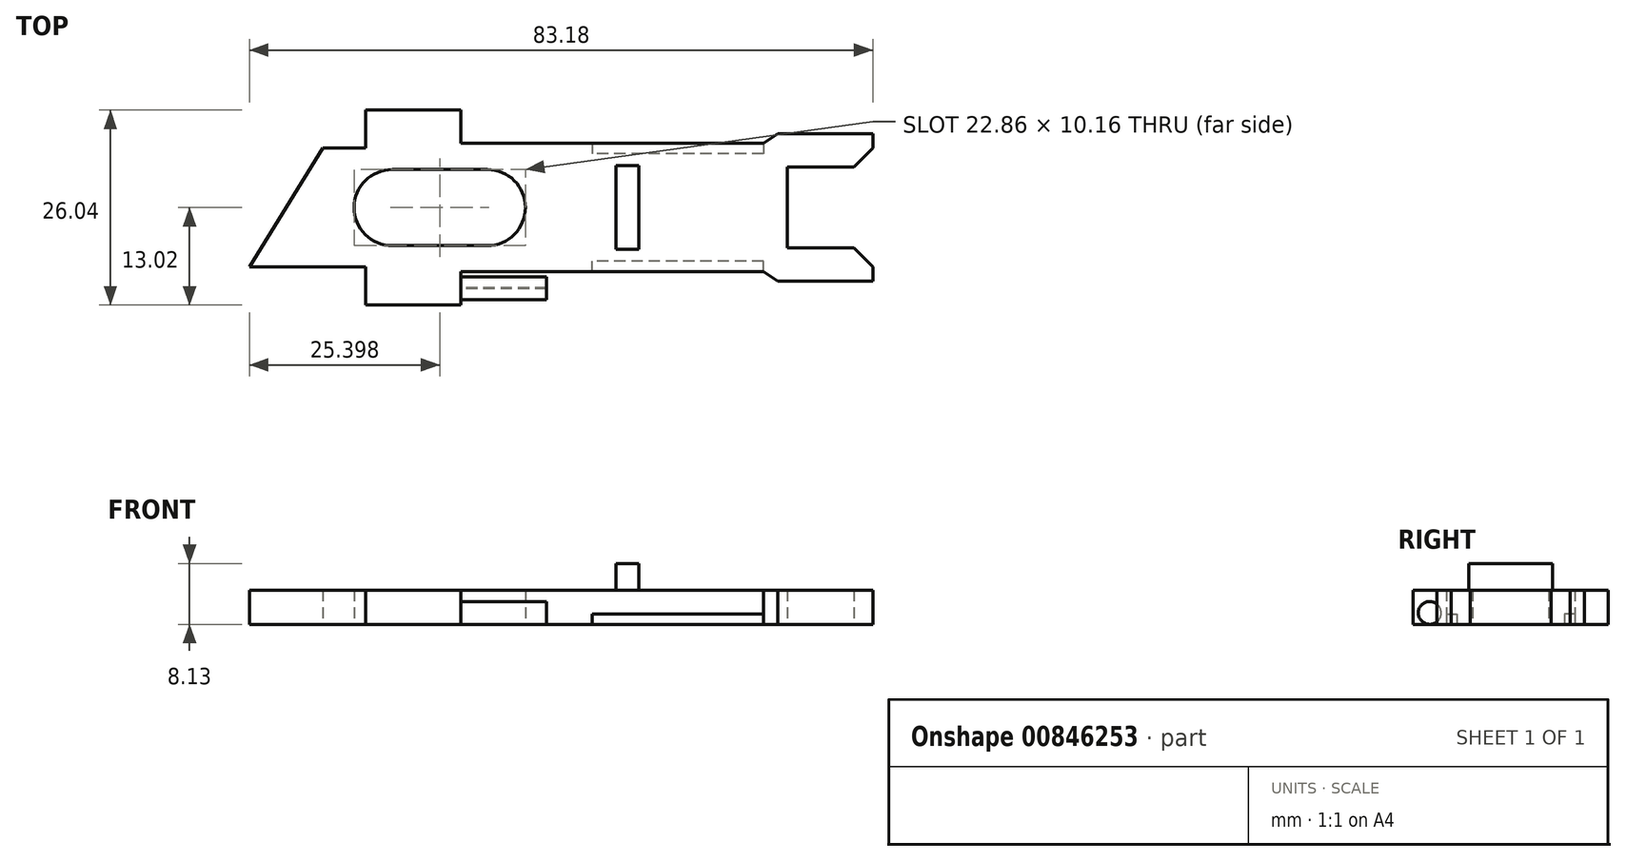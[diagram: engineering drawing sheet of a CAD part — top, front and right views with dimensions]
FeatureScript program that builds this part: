
annotation { "Feature Type Name" : "Feature", "Feature Type Description" : "" }
export const myFeature = defineFeature(function(context is Context, id is Id, definition is map)
    precondition{}
    {
        {
            var Q0;
            Q0=qCreatedBy(makeId("Top.planeOp"),FACE);
            var sketch = newSketch(context, id + "F0", { "sketchPlane" : qUnion([Q0])});
            skLineSegment(sketch, "E0", {"start": v(31.34, -9.84) * mm, "end": v(18.64, -9.84) * mm});
            skLineSegment(sketch, "E1", {"start": v(18.64, -9.84) * mm, "end": v(16.74, -8.57) * mm});
            skLineSegment(sketch, "E2", {"start": v(16.74, -8.57) * mm, "end": v(-23.65, -8.57) * mm});
            skLineSegment(sketch, "E3", {"start": v(-23.65, -8.57) * mm, "end": v(-23.65, -13.02) * mm});
            skLineSegment(sketch, "E4", {"start": v(-23.65, -13.02) * mm, "end": v(-36.35, -13.02) * mm});
            skLineSegment(sketch, "E5", {"start": v(-36.35, -13.02) * mm, "end": v(-36.35, -7.94) * mm});
            skLineSegment(sketch, "E6", {"start": v(-36.35, -7.94) * mm, "end": v(-51.84, -7.94) * mm});
            skLineSegment(sketch, "E7", {"start": v(-51.84, -7.94) * mm, "end": v(-42.06, 7.94) * mm});
            skLineSegment(sketch, "E8", {"start": v(-42.06, 7.94) * mm, "end": v(-36.35, 7.94) * mm});
            skLineSegment(sketch, "E9", {"start": v(-36.35, 7.94) * mm, "end": v(-36.35, 13.02) * mm});
            skLineSegment(sketch, "E10", {"start": v(-36.35, 13.02) * mm, "end": v(-23.65, 13.02) * mm});
            skLineSegment(sketch, "E11", {"start": v(-23.65, 13.02) * mm, "end": v(-23.65, 8.57) * mm});
            skLineSegment(sketch, "E12", {"start": v(-23.65, 8.57) * mm, "end": v(16.74, 8.57) * mm});
            skLineSegment(sketch, "E13", {"start": v(16.74, 8.57) * mm, "end": v(18.64, 9.84) * mm});
            skLineSegment(sketch, "E14", {"start": v(18.64, 9.84) * mm, "end": v(31.34, 9.84) * mm});
            skLineSegment(sketch, "E15", {"start": v(31.34, 9.84) * mm, "end": v(31.34, 7.94) * mm});
            skLineSegment(sketch, "E16", {"start": v(31.34, 7.94) * mm, "end": v(28.8, 5.4) * mm});
            skLineSegment(sketch, "E17", {"start": v(28.8, 5.4) * mm, "end": v(19.91, 5.4) * mm});
            skLineSegment(sketch, "E18", {"start": v(19.91, 5.4) * mm, "end": v(19.91, -5.4) * mm});
            skLineSegment(sketch, "E19", {"start": v(19.91, -5.4) * mm, "end": v(28.8, -5.4) * mm});
            skLineSegment(sketch, "E20", {"start": v(28.8, -5.4) * mm, "end": v(31.34, -7.94) * mm});
            skLineSegment(sketch, "E21", {"start": v(31.34, -7.94) * mm, "end": v(31.34, -9.84) * mm});
            skPoint(sketch, "E22", {"position": v(-20.1, 0) * mm});
            skPoint(sketch, "E23", {"position": v(-32.8, 0) * mm});
            skArc(sketch, "E24", {"start": v(-20.1, 5.08) * mm, "mid": v(-15.01, 0) * mm, "end": v(-20.1, -5.08) * mm});
            skArc(sketch, "E25", {"start": v(-32.8, 5.08) * mm, "mid": v(-37.87, 0) * mm, "end": v(-32.8, -5.08) * mm});
            skLineSegment(sketch, "E26", {"start": v(-32.8, 5.08) * mm, "end": v(-20.1, 5.08) * mm});
            skLineSegment(sketch, "E27", {"start": v(-32.8, -5.08) * mm, "end": v(-20.1, -5.08) * mm});
            skPoint(sketch, "E28", {"position": v(-1.42, 0) * mm});
            skLineSegment(sketch, "E29.bottom", {"start": v(-2.95, 5.59) * mm, "end": v(0.1, 5.59) * mm});
            skLineSegment(sketch, "E29.top", {"start": v(-2.95, -5.59) * mm, "end": v(0.1, -5.59) * mm});
            skLineSegment(sketch, "E29.left", {"start": v(-2.95, 5.59) * mm, "end": v(-2.95, -5.59) * mm});
            skLineSegment(sketch, "E29.right", {"start": v(0.1, 5.59) * mm, "end": v(0.1, -5.59) * mm});
            skSolve(sketch);
        }
        {
            var Q0;
            Q0 = qSketchRegion(id + "F0", true);
            extrude(context, id + "F1", {"entities" : qUnion([Q0]), "depth" : 4.57 * mm, "offsetDistance" : 25.4 * mm});
        }
        {
            var Q0;
            Q0=makeQuery(id+"F0.imprint","IMPRINT",FACE,{"disambiguationData":[TD([[makeQuery(id+"F0.imprint","IMPRINT",EDGE,{"derivedFrom":sQuery(id+"F0.wireOp",EDGE,"E29.bottom")}),-1.0]])]});
            extrude(context, id + "F2", {"entities" : qUnion([Q0]), "operationType" : NewBodyOperationType.ADD, "depth" : 8.13 * mm, "offsetDistance" : 25.4 * mm});
        }
        {
            var Q0;
            Q0=makeQuery(id+"F1.opExtrude","SWEPT_FACE",FACE,{"disambiguationData":[OSD([sQuery(id+"F0.wireOp",EDGE,"E3")])]});
            var sketch = newSketch(context, id + "F3", { "sketchPlane" : qUnion([Q0])});
            skCircle(sketch, "E30", {"center": v(-10.8, 1.52) * mm, "radius": 1.53 * mm});
            skPoint(sketch, "E30.centerSnap0", {"position": v(-10.8, 0) * mm});
            skSolve(sketch);
        }
        {
            var Q0;
            {var subQ0=sQuery(id+"F3.wireOp",EDGE,"E30");var subQ1=makeQuery(id+"F1.opExtrude","CAP_EDGE",EDGE,{"disambiguationData":[OSD([sQuery(id+"F0.wireOp",EDGE,"E3")])],"isStart":true});var subQ2=makeQuery(id+"F3.imprint","INTERSECT",VERTEX,{"disambiguationData":[OD(0.0)],"derivedFrom":[subQ1,subQ0]});Q0=makeQuery(id+"F3.imprint","IMPRINT",FACE,{"disambiguationData":[TD([[makeQuery(id+"F3.imprint","IMPRINT",EDGE,{"disambiguationData":[TD([[subQ2,-1.0]])],"derivedFrom":subQ0}),1.0]])]});}
            extrude(context, id + "F4", {"entities" : qUnion([Q0]), "operationType" : NewBodyOperationType.ADD, "depth" : 11.43 * mm, "offsetDistance" : 25.4 * mm});
        }
        {
            var Q0;
            {var subQ0=sQuery(id+"F0.wireOp",EDGE,"E3");var subQ1=sQuery(id+"F0.wireOp",EDGE,"E29.right");var subQ2=sQuery(id+"F0.wireOp",EDGE,"E29.left");var subQ3=sQuery(id+"F0.wireOp",EDGE,"E29.top");var subQ4=sQuery(id+"F0.wireOp",EDGE,"E29.bottom");Q0=makeQuery(id+"F4.boolean.opBoolean","MERGE",FACE,{"derivedFrom":[makeQuery(id+"F2.boolean.opBoolean","MERGE",FACE,{"derivedFrom":[makeQuery(id+"F1.opExtrude","CAP_FACE",FACE,{"disambiguationData":[OSD([sQuery(id+"F0.wireOp",EDGE,"E0"),sQuery(id+"F0.wireOp",EDGE,"E1"),sQuery(id+"F0.wireOp",EDGE,"E2"),subQ0,sQuery(id+"F0.wireOp",EDGE,"E4"),sQuery(id+"F0.wireOp",EDGE,"E5"),sQuery(id+"F0.wireOp",EDGE,"E6"),sQuery(id+"F0.wireOp",EDGE,"E7"),sQuery(id+"F0.wireOp",EDGE,"E8"),sQuery(id+"F0.wireOp",EDGE,"E9"),sQuery(id+"F0.wireOp",EDGE,"E10"),sQuery(id+"F0.wireOp",EDGE,"E11"),sQuery(id+"F0.wireOp",EDGE,"E12"),sQuery(id+"F0.wireOp",EDGE,"E13"),sQuery(id+"F0.wireOp",EDGE,"E14"),sQuery(id+"F0.wireOp",EDGE,"E15"),sQuery(id+"F0.wireOp",EDGE,"E16"),sQuery(id+"F0.wireOp",EDGE,"E17"),sQuery(id+"F0.wireOp",EDGE,"E18"),sQuery(id+"F0.wireOp",EDGE,"E19"),sQuery(id+"F0.wireOp",EDGE,"E20"),sQuery(id+"F0.wireOp",EDGE,"E21"),sQuery(id+"F0.wireOp",EDGE,"E24"),sQuery(id+"F0.wireOp",EDGE,"E25"),sQuery(id+"F0.wireOp",EDGE,"E26"),sQuery(id+"F0.wireOp",EDGE,"E27"),subQ4,subQ3,subQ2,subQ1])],"isStart":true}),makeQuery(id+"F2.opExtrude","CAP_FACE",FACE,{"disambiguationData":[OSD([subQ4,subQ3,subQ2,subQ1])],"isStart":true})]}),makeQuery(id+"F4.opExtrude","SWEPT_FACE",FACE,{"disambiguationData":[OSD([subQ0])]})]});}
            var sketch = newSketch(context, id + "F5", { "sketchPlane" : qUnion([Q0])});
            skLineSegment(sketch, "E31.bottom", {"start": v(16.74, -8.57) * mm, "end": v(-6.12, -8.57) * mm});
            skLineSegment(sketch, "E31.top", {"start": v(16.74, -7.18) * mm, "end": v(-6.12, -7.18) * mm});
            skLineSegment(sketch, "E31.left", {"start": v(16.74, -8.57) * mm, "end": v(16.74, -7.18) * mm});
            skLineSegment(sketch, "E31.right", {"start": v(-6.12, -8.57) * mm, "end": v(-6.12, -7.18) * mm});
            skLineSegment(sketch, "E32.bottom", {"start": v(16.74, 8.57) * mm, "end": v(-6.12, 8.57) * mm});
            skLineSegment(sketch, "E32.top", {"start": v(16.74, 7.18) * mm, "end": v(-6.12, 7.18) * mm});
            skLineSegment(sketch, "E32.left", {"start": v(16.74, 8.57) * mm, "end": v(16.74, 7.18) * mm});
            skLineSegment(sketch, "E32.right", {"start": v(-6.12, 8.57) * mm, "end": v(-6.12, 7.18) * mm});
            skSolve(sketch);
        }
        {
            var Q0;
            Q0=makeQuery(id+"F5.imprint","IMPRINT",FACE,{"disambiguationData":[TD([[makeQuery(id+"F5.imprint","IMPRINT",EDGE,{"derivedFrom":sQuery(id+"F5.wireOp",EDGE,"E32.bottom")}),1.0]])]});
            extrude(context, id + "F6", {"entities" : qUnion([Q0]), "operationType" : NewBodyOperationType.REMOVE, "oppositeDirection" : true, "depth" : 1.4 * mm, "offsetDistance" : 25.4 * mm});
        }
        {
            var Q0;
            Q0=makeQuery(id+"F5.imprint","IMPRINT",FACE,{"disambiguationData":[TD([[makeQuery(id+"F5.imprint","IMPRINT",EDGE,{"derivedFrom":sQuery(id+"F5.wireOp",EDGE,"E31.bottom")}),1.0]])]});
            extrude(context, id + "F7", {"entities" : qUnion([Q0]), "operationType" : NewBodyOperationType.REMOVE, "oppositeDirection" : true, "depth" : 1.4 * mm, "offsetDistance" : 25.4 * mm});
        }
    });
